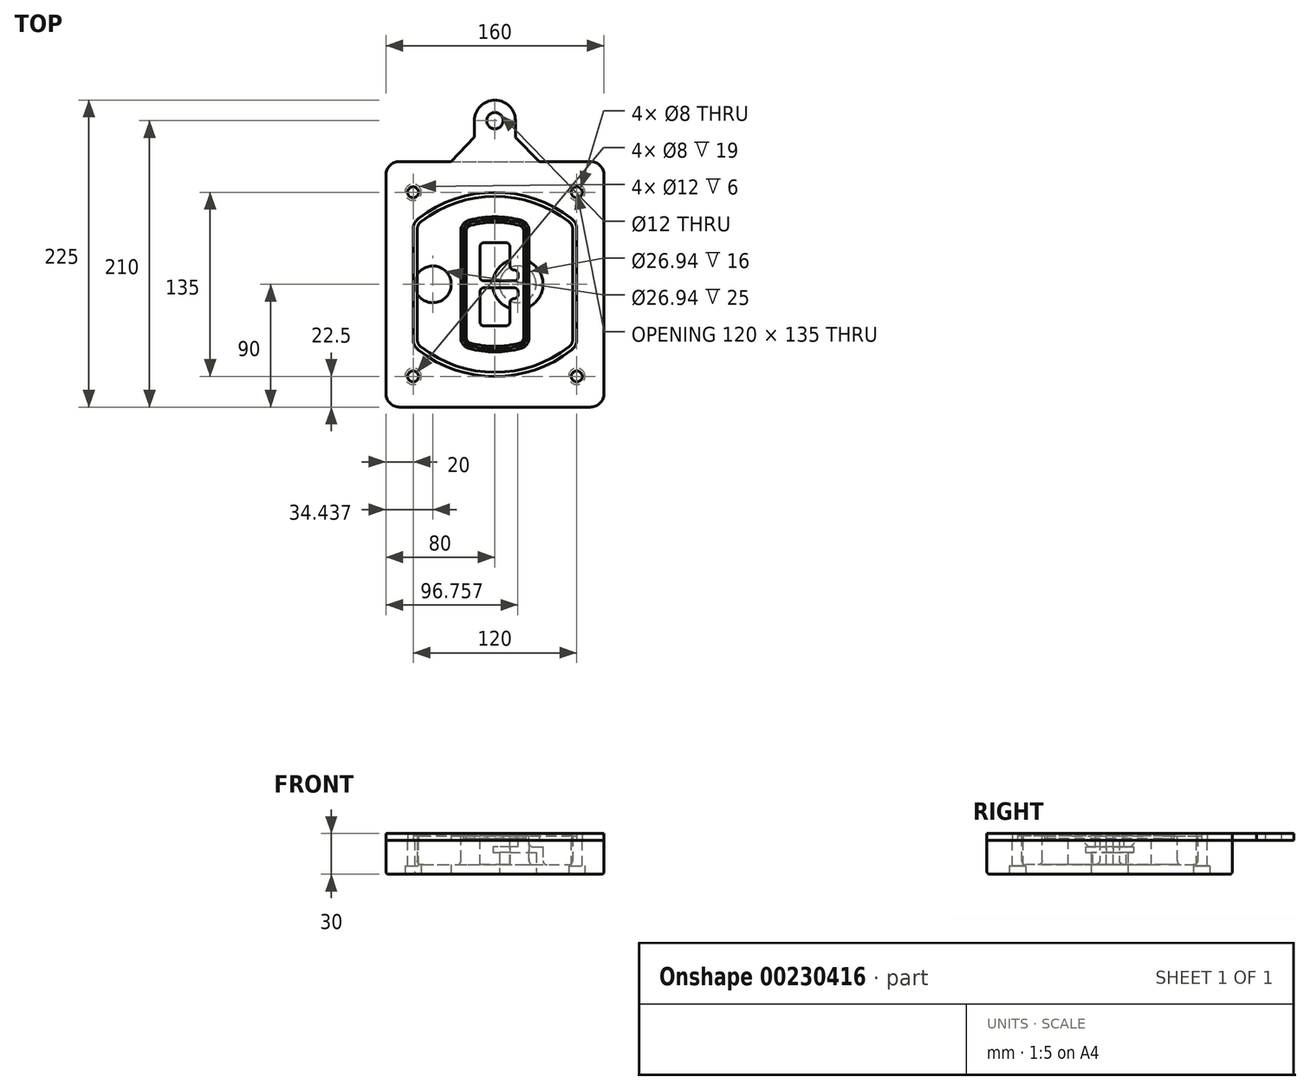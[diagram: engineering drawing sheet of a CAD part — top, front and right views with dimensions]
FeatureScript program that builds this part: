
annotation { "Feature Type Name" : "Feature", "Feature Type Description" : "" }
export const myFeature = defineFeature(function(context is Context, id is Id, definition is map)
    precondition{}
    {
        {
            var Q0;
            Q0=qCreatedBy(makeId("Top.planeOp"),FACE);
            var sketch = newSketch(context, id + "F0", { "sketchPlane" : qUnion([Q0])});
            skPoint(sketch, "E0.rect.middle", {"position": v(0, 0) * mm});
            skLineSegment(sketch, "E1.bottom", {"start": v(-70, -90) * mm, "end": v(70, -90) * mm});
            skLineSegment(sketch, "E1.top", {"start": v(-70, 90) * mm, "end": v(70, 90) * mm});
            skLineSegment(sketch, "E1.left", {"start": v(-80, -80) * mm, "end": v(-80, 80) * mm});
            skLineSegment(sketch, "E1.right", {"start": v(80, -80) * mm, "end": v(80, 80) * mm});
            skLineSegment(sketch, "E2", {"start": v(-80, 90) * mm, "end": v(80, -90) * mm, "construction": true});
            skLineSegment(sketch, "E3", {"start": v(80, 90) * mm, "end": v(-80, -90) * mm, "construction": true});
            skCircle(sketch, "E4", {"center": v(-60, 67.5) * mm, "radius": 4 * mm});
            skCircle(sketch, "E5", {"center": v(60, 67.5) * mm, "radius": 4 * mm});
            skCircle(sketch, "E6", {"center": v(60, -67.5) * mm, "radius": 4 * mm});
            skCircle(sketch, "E7", {"center": v(-60, -67.5) * mm, "radius": 4 * mm});
            skLineSegment(sketch, "E8", {"start": v(-60, 67.5) * mm, "end": v(60, 67.5) * mm, "construction": true});
            skLineSegment(sketch, "E9", {"start": v(60, 67.5) * mm, "end": v(60, -67.5) * mm, "construction": true});
            skLineSegment(sketch, "E10", {"start": v(60, -67.5) * mm, "end": v(-60, -67.5) * mm, "construction": true});
            skLineSegment(sketch, "E11", {"start": v(-60, -67.5) * mm, "end": v(-60, 67.5) * mm, "construction": true});
            skLineSegment(sketch, "E12", {"start": v(-60, 40.3) * mm, "end": v(-60, -40.3) * mm});
            skLineSegment(sketch, "E13", {"start": v(60, 40.3) * mm, "end": v(60, -40.3) * mm});
            skArc(sketch, "E14", {"start": v(56.15, 48.18) * mm, "mid": v(0, 67.5) * mm, "end": v(-56.15, 48.18) * mm});
            skArc(sketch, "E15", {"start": v(-56.15, -48.18) * mm, "mid": v(0, -67.5) * mm, "end": v(56.15, -48.18) * mm});
            skLineSegment(sketch, "E16", {"start": v(-60, 0) * mm, "end": v(60, 0) * mm, "construction": true});
            skPoint(sketch, "E17.visualSharp", {"position": v(-60, -45) * mm});
            skArc(sketch, "E17.filletArc", {"start": v(-60, -40.3) * mm, "mid": v(-58.99, -44.68) * mm, "end": v(-56.15, -48.18) * mm});
            skPoint(sketch, "E18.visualSharp", {"position": v(-60, 45) * mm});
            skArc(sketch, "E18.filletArc", {"start": v(-56.15, 48.18) * mm, "mid": v(-58.99, 44.68) * mm, "end": v(-60, 40.3) * mm});
            skPoint(sketch, "E19.visualSharp", {"position": v(60, 45) * mm});
            skArc(sketch, "E19.filletArc", {"start": v(60, 40.3) * mm, "mid": v(58.99, 44.68) * mm, "end": v(56.15, 48.18) * mm});
            skPoint(sketch, "E20.visualSharp", {"position": v(60, -45) * mm});
            skArc(sketch, "E20.filletArc", {"start": v(56.15, -48.18) * mm, "mid": v(58.99, -44.68) * mm, "end": v(60, -40.3) * mm});
            skPoint(sketch, "E21.visualSharp", {"position": v(-80, 90) * mm});
            skArc(sketch, "E21.filletArc", {"start": v(-70, 90) * mm, "mid": v(-77.07, 87.07) * mm, "end": v(-80, 80) * mm});
            skPoint(sketch, "E22.visualSharp", {"position": v(80, 90) * mm});
            skArc(sketch, "E22.filletArc", {"start": v(80, 80) * mm, "mid": v(77.07, 87.07) * mm, "end": v(70, 90) * mm});
            skPoint(sketch, "E23.visualSharp", {"position": v(80, -90) * mm});
            skArc(sketch, "E23.filletArc", {"start": v(70, -90) * mm, "mid": v(77.07, -87.07) * mm, "end": v(80, -80) * mm});
            skPoint(sketch, "E24.visualSharp", {"position": v(-80, -90) * mm});
            skArc(sketch, "E24.filletArc", {"start": v(-80, -80) * mm, "mid": v(-77.07, -87.07) * mm, "end": v(-70, -90) * mm});
            skArc(sketch, "E25.0", {"start": v(57, 40.3) * mm, "mid": v(56.3, 43.36) * mm, "end": v(54.3, 45.81) * mm});
            skLineSegment(sketch, "E25.1", {"start": v(57, 40.3) * mm, "end": v(57, -40.3) * mm});
            skArc(sketch, "E25.2", {"start": v(54.3, -45.81) * mm, "mid": v(56.3, -43.36) * mm, "end": v(57, -40.3) * mm});
            skArc(sketch, "E25.3", {"start": v(-54.3, -45.81) * mm, "mid": v(0, -64.5) * mm, "end": v(54.3, -45.81) * mm});
            skArc(sketch, "E25.4", {"start": v(-57, -40.3) * mm, "mid": v(-56.3, -43.36) * mm, "end": v(-54.3, -45.81) * mm});
            skArc(sketch, "E25.5", {"start": v(54.3, 45.81) * mm, "mid": v(0, 64.5) * mm, "end": v(-54.3, 45.81) * mm});
            skLineSegment(sketch, "E25.6", {"start": v(-57, 40.3) * mm, "end": v(-57, -40.3) * mm});
            skArc(sketch, "E25.7", {"start": v(-54.3, 45.81) * mm, "mid": v(-56.3, 43.36) * mm, "end": v(-57, 40.3) * mm});
            skArc(sketch, "E26.0", {"start": v(-58.62, 51.33) * mm, "mid": v(-62.58, 46.43) * mm, "end": v(-64, 40.3) * mm});
            skArc(sketch, "E26.1", {"start": v(58.62, 51.33) * mm, "mid": v(0, 71.5) * mm, "end": v(-58.62, 51.33) * mm});
            skArc(sketch, "E26.2", {"start": v(64, 40.3) * mm, "mid": v(62.58, 46.43) * mm, "end": v(58.62, 51.33) * mm});
            skLineSegment(sketch, "E26.3", {"start": v(64, 40.3) * mm, "end": v(64, -40.3) * mm});
            skArc(sketch, "E26.4", {"start": v(58.62, -51.33) * mm, "mid": v(62.58, -46.43) * mm, "end": v(64, -40.3) * mm});
            skLineSegment(sketch, "E26.5", {"start": v(-64, 40.3) * mm, "end": v(-64, -40.3) * mm});
            skArc(sketch, "E26.6", {"start": v(-58.62, -51.33) * mm, "mid": v(0, -71.5) * mm, "end": v(58.62, -51.33) * mm});
            skArc(sketch, "E26.7", {"start": v(-64, -40.3) * mm, "mid": v(-62.58, -46.43) * mm, "end": v(-58.62, -51.33) * mm});
            skSolve(sketch);
        }
        {
            var Q0;
            Q0=makeQuery(id+"F0.imprint","IMPRINT",FACE,{"disambiguationData":[TD([[makeQuery(id+"F0.imprint","IMPRINT",EDGE,{"derivedFrom":sQuery(id+"F0.wireOp",EDGE,"E1.bottom")}),1.0]])]});
            var Q1;
            Q1=makeQuery(id+"F0.imprint","IMPRINT",FACE,{"disambiguationData":[TD([[makeQuery(id+"F0.imprint","IMPRINT",EDGE,{"derivedFrom":sQuery(id+"F0.wireOp",EDGE,"E12")}),1.0]])]});
            var Q2;
            Q2=makeQuery(id+"F0.imprint","IMPRINT",FACE,{"disambiguationData":[TD([[makeQuery(id+"F0.imprint","IMPRINT",EDGE,{"derivedFrom":sQuery(id+"F0.wireOp",EDGE,"E25.0")}),1.0]])]});
            var Q3;
            Q3=makeQuery(id+"F0.imprint","IMPRINT",FACE,{"disambiguationData":[TD([[makeQuery(id+"F0.imprint","IMPRINT",EDGE,{"derivedFrom":sQuery(id+"F0.wireOp",EDGE,"E12")}),-1.0]])]});
            extrude(context, id + "F1", {"entities" : qUnion([Q0, Q1, Q2, Q3]), "oppositeDirection" : true, "depth" : 25 * mm});
        }
        {
            var Q0;
            Q0=makeQuery(id+"F0.imprint","IMPRINT",FACE,{"disambiguationData":[TD([[makeQuery(id+"F0.imprint","IMPRINT",EDGE,{"derivedFrom":sQuery(id+"F0.wireOp",EDGE,"E12")}),1.0]])]});
            extrude(context, id + "F2", {"entities" : qUnion([Q0]), "operationType" : NewBodyOperationType.ADD, "depth" : 3 * mm});
        }
        {
            var Q0;
            Q0=makeQuery(id+"F0.imprint","IMPRINT",FACE,{"disambiguationData":[TD([[makeQuery(id+"F0.imprint","IMPRINT",EDGE,{"derivedFrom":sQuery(id+"F0.wireOp",EDGE,"E25.0")}),1.0]])]});
            extrude(context, id + "F3", {"entities" : qUnion([Q0]), "operationType" : NewBodyOperationType.REMOVE, "oppositeDirection" : true, "depth" : 18 * mm});
        }
        {
            var Q0;
            Q0=makeQuery(id+"F2.opExtrude","CAP_FACE",FACE,{"disambiguationData":[OSD([sQuery(id+"F0.wireOp",EDGE,"E12"),sQuery(id+"F0.wireOp",EDGE,"E13"),sQuery(id+"F0.wireOp",EDGE,"E14"),sQuery(id+"F0.wireOp",EDGE,"E15"),sQuery(id+"F0.wireOp",EDGE,"E17.filletArc"),sQuery(id+"F0.wireOp",EDGE,"E18.filletArc"),sQuery(id+"F0.wireOp",EDGE,"E19.filletArc"),sQuery(id+"F0.wireOp",EDGE,"E20.filletArc"),sQuery(id+"F0.wireOp",EDGE,"E25.0"),sQuery(id+"F0.wireOp",EDGE,"E25.1"),sQuery(id+"F0.wireOp",EDGE,"E25.2"),sQuery(id+"F0.wireOp",EDGE,"E25.3"),sQuery(id+"F0.wireOp",EDGE,"E25.4"),sQuery(id+"F0.wireOp",EDGE,"E25.5"),sQuery(id+"F0.wireOp",EDGE,"E25.6"),sQuery(id+"F0.wireOp",EDGE,"E25.7")])],"isStart":false});
            var sketch = newSketch(context, id + "F4", { "sketchPlane" : qUnion([Q0])});
            skArc(sketch, "E27.0", {"start": v(-19.08, -46.97) * mm, "mid": v(0, -49.5) * mm, "end": v(19.08, -46.97) * mm});
            skArc(sketch, "E28.0", {"start": v(19.08, 46.97) * mm, "mid": v(0, 49.5) * mm, "end": v(-19.08, 46.97) * mm});
            skLineSegment(sketch, "E29", {"start": v(-25, 39.25) * mm, "end": v(-25, -39.25) * mm});
            skLineSegment(sketch, "E30", {"start": v(25, 39.25) * mm, "end": v(25, -39.25) * mm});
            skLineSegment(sketch, "E31", {"start": v(-25, 45.1) * mm, "end": v(25, 45.1) * mm, "construction": true});
            skLineSegment(sketch, "E32", {"start": v(-25, -45.1) * mm, "end": v(25, -45.1) * mm, "construction": true});
            skPoint(sketch, "E33.visualSharp", {"position": v(-25, 45.1) * mm});
            skArc(sketch, "E33.filletArc", {"start": v(-19.08, 46.97) * mm, "mid": v(-23.35, 44.11) * mm, "end": v(-25, 39.25) * mm});
            skPoint(sketch, "E34.visualSharp", {"position": v(25, 45.1) * mm});
            skArc(sketch, "E34.filletArc", {"start": v(25, 39.25) * mm, "mid": v(23.35, 44.11) * mm, "end": v(19.08, 46.97) * mm});
            skPoint(sketch, "E35.visualSharp", {"position": v(25, -45.1) * mm});
            skArc(sketch, "E35.filletArc", {"start": v(19.08, -46.97) * mm, "mid": v(23.35, -44.11) * mm, "end": v(25, -39.25) * mm});
            skPoint(sketch, "E36.visualSharp", {"position": v(-25, -45.1) * mm});
            skArc(sketch, "E36.filletArc", {"start": v(-25, -39.25) * mm, "mid": v(-23.35, -44.11) * mm, "end": v(-19.08, -46.97) * mm});
            skArc(sketch, "E37.0", {"start": v(54.3, 45.81) * mm, "mid": v(0, 64.5) * mm, "end": v(-54.3, 45.81) * mm});
            skArc(sketch, "E37.1", {"start": v(-54.3, 45.81) * mm, "mid": v(-56.3, 43.36) * mm, "end": v(-57, 40.3) * mm});
            skLineSegment(sketch, "E37.2", {"start": v(-57, 40.3) * mm, "end": v(-57, -40.3) * mm});
            skArc(sketch, "E37.3", {"start": v(-57, -40.3) * mm, "mid": v(-56.3, -43.36) * mm, "end": v(-54.3, -45.81) * mm});
            skArc(sketch, "E37.4", {"start": v(-54.3, -45.81) * mm, "mid": v(0, -64.5) * mm, "end": v(54.3, -45.81) * mm});
            skArc(sketch, "E37.5", {"start": v(54.3, -45.81) * mm, "mid": v(56.3, -43.36) * mm, "end": v(57, -40.3) * mm});
            skLineSegment(sketch, "E37.6", {"start": v(57, 40.3) * mm, "end": v(57, -40.3) * mm});
            skArc(sketch, "E37.7", {"start": v(57, 40.3) * mm, "mid": v(56.3, 43.36) * mm, "end": v(54.3, 45.81) * mm});
            skLineSegment(sketch, "E38.0", {"start": v(23, 39.25) * mm, "end": v(23, -39.25) * mm});
            skArc(sketch, "E38.1", {"start": v(18.56, -45.04) * mm, "mid": v(21.76, -42.9) * mm, "end": v(23, -39.25) * mm});
            skArc(sketch, "E38.2", {"start": v(-18.56, -45.04) * mm, "mid": v(0, -47.5) * mm, "end": v(18.56, -45.04) * mm});
            skArc(sketch, "E38.3", {"start": v(-23, -39.25) * mm, "mid": v(-21.76, -42.9) * mm, "end": v(-18.56, -45.04) * mm});
            skLineSegment(sketch, "E38.4", {"start": v(-23, 39.25) * mm, "end": v(-23, -39.25) * mm});
            skArc(sketch, "E38.5", {"start": v(23, 39.25) * mm, "mid": v(21.76, 42.9) * mm, "end": v(18.56, 45.04) * mm});
            skArc(sketch, "E38.6", {"start": v(-18.56, 45.04) * mm, "mid": v(-21.76, 42.9) * mm, "end": v(-23, 39.25) * mm});
            skArc(sketch, "E38.7", {"start": v(18.56, 45.04) * mm, "mid": v(0, 47.5) * mm, "end": v(-18.56, 45.04) * mm});
            skArc(sketch, "E39.0", {"start": v(21, 39.25) * mm, "mid": v(20.18, 41.68) * mm, "end": v(18.04, 43.1) * mm});
            skLineSegment(sketch, "E39.1", {"start": v(21, 39.25) * mm, "end": v(21, -39.25) * mm});
            skArc(sketch, "E39.2", {"start": v(18.04, -43.1) * mm, "mid": v(20.18, -41.68) * mm, "end": v(21, -39.25) * mm});
            skArc(sketch, "E39.3", {"start": v(-18.04, -43.1) * mm, "mid": v(0, -45.5) * mm, "end": v(18.04, -43.1) * mm});
            skArc(sketch, "E39.4", {"start": v(-21, -39.25) * mm, "mid": v(-20.18, -41.68) * mm, "end": v(-18.04, -43.1) * mm});
            skArc(sketch, "E39.5", {"start": v(18.04, 43.1) * mm, "mid": v(0, 45.5) * mm, "end": v(-18.04, 43.1) * mm});
            skLineSegment(sketch, "E39.6", {"start": v(-21, 39.25) * mm, "end": v(-21, -39.25) * mm});
            skArc(sketch, "E39.7", {"start": v(-18.04, 43.1) * mm, "mid": v(-20.18, 41.68) * mm, "end": v(-21, 39.25) * mm});
            skLineSegment(sketch, "E40", {"start": v(-25, 0) * mm, "end": v(25, 0) * mm, "construction": true});
            skLineSegment(sketch, "E41", {"start": v(-11, 5.5) * mm, "end": v(-11, 27.5) * mm});
            skLineSegment(sketch, "E42", {"start": v(-8, 30.5) * mm, "end": v(8, 30.5) * mm});
            skLineSegment(sketch, "E43", {"start": v(11, 27.5) * mm, "end": v(11, 13.5) * mm});
            skLineSegment(sketch, "E44", {"start": v(14, 10.5) * mm, "end": v(14, 10.5) * mm});
            skLineSegment(sketch, "E45", {"start": v(17, 7.5) * mm, "end": v(17, 5.5) * mm});
            skLineSegment(sketch, "E46", {"start": v(14, 2.5) * mm, "end": v(-8, 2.5) * mm});
            skPoint(sketch, "E47.visualSharp", {"position": v(-11, 30.5) * mm});
            skArc(sketch, "E47.filletArc", {"start": v(-8, 30.5) * mm, "mid": v(-10.12, 29.62) * mm, "end": v(-11, 27.5) * mm});
            skPoint(sketch, "E48.visualSharp", {"position": v(11, 30.5) * mm});
            skArc(sketch, "E48.filletArc", {"start": v(11, 27.5) * mm, "mid": v(10.12, 29.62) * mm, "end": v(8, 30.5) * mm});
            skPoint(sketch, "E49.visualSharp", {"position": v(11, 10.5) * mm});
            skArc(sketch, "E49.filletArc", {"start": v(11, 13.5) * mm, "mid": v(11.88, 11.38) * mm, "end": v(14, 10.5) * mm});
            skPoint(sketch, "E50.visualSharp", {"position": v(17, 10.5) * mm});
            skArc(sketch, "E50.filletArc", {"start": v(17, 7.5) * mm, "mid": v(16.12, 9.62) * mm, "end": v(14, 10.5) * mm});
            skPoint(sketch, "E51.visualSharp", {"position": v(17, 2.5) * mm});
            skArc(sketch, "E51.filletArc", {"start": v(14, 2.5) * mm, "mid": v(16.12, 3.38) * mm, "end": v(17, 5.5) * mm});
            skPoint(sketch, "E52.visualSharp", {"position": v(-11, 2.5) * mm});
            skArc(sketch, "E52.filletArc", {"start": v(-11, 5.5) * mm, "mid": v(-10.12, 3.38) * mm, "end": v(-8, 2.5) * mm});
            skLineSegment(sketch, "E53.0.MirrorCS", {"start": v(14, -2.5) * mm, "end": v(-8, -2.5) * mm});
            skArc(sketch, "E54.0.MirrorCS", {"start": v(-11, -5.5) * mm, "mid": v(-10.12, -3.38) * mm, "end": v(-8, -2.5) * mm});
            skLineSegment(sketch, "E55.0.MirrorCS", {"start": v(-11, -5.5) * mm, "end": v(-11, -27.5) * mm});
            skArc(sketch, "E56.0.MirrorCS", {"start": v(-8, -30.5) * mm, "mid": v(-10.12, -29.62) * mm, "end": v(-11, -27.5) * mm});
            skLineSegment(sketch, "E57.0.MirrorCS", {"start": v(-8, -30.5) * mm, "end": v(8, -30.5) * mm});
            skArc(sketch, "E58.0.MirrorCS", {"start": v(11, -27.5) * mm, "mid": v(10.12, -29.62) * mm, "end": v(8, -30.5) * mm});
            skLineSegment(sketch, "E59.0.MirrorCS", {"start": v(11, -27.5) * mm, "end": v(11, -13.5) * mm});
            skArc(sketch, "E60.0.MirrorCS", {"start": v(11, -13.5) * mm, "mid": v(11.88, -11.38) * mm, "end": v(14, -10.5) * mm});
            skArc(sketch, "E61.0.MirrorCS", {"start": v(17, -7.5) * mm, "mid": v(16.12, -9.62) * mm, "end": v(14, -10.5) * mm});
            skLineSegment(sketch, "E62.0.MirrorCS", {"start": v(17, -7.5) * mm, "end": v(17, -5.5) * mm});
            skArc(sketch, "E63.0.MirrorCS", {"start": v(14, -2.5) * mm, "mid": v(16.12, -3.38) * mm, "end": v(17, -5.5) * mm});
            skSolve(sketch);
        }
        {
            var Q0;
            Q0=makeQuery(id+"F4.imprint","IMPRINT",FACE,{"disambiguationData":[TD([[makeQuery(id+"F4.imprint","IMPRINT",EDGE,{"derivedFrom":sQuery(id+"F4.wireOp",EDGE,"E27.0")}),1.0]])]});
            var Q1;
            Q1=makeQuery(id+"F4.imprint","IMPRINT",FACE,{"disambiguationData":[TD([[makeQuery(id+"F4.imprint","IMPRINT",EDGE,{"derivedFrom":sQuery(id+"F4.wireOp",EDGE,"E38.0")}),-1.0]])]});
            var Q2;
            Q2=makeQuery(id+"F4.imprint","IMPRINT",FACE,{"disambiguationData":[TD([[makeQuery(id+"F4.imprint","IMPRINT",EDGE,{"derivedFrom":sQuery(id+"F4.wireOp",EDGE,"E39.0")}),1.0]])]});
            extrude(context, id + "F5", {"entities" : qUnion([Q0, Q1, Q2]), "operationType" : NewBodyOperationType.ADD, "endBound" : BoundingType.UP_TO_NEXT, "oppositeDirection" : true, "depth" : 25 * mm});
        }
        {
            var Q0;
            Q0=makeQuery(id+"F4.imprint","IMPRINT",FACE,{"disambiguationData":[TD([[makeQuery(id+"F4.imprint","IMPRINT",EDGE,{"derivedFrom":sQuery(id+"F4.wireOp",EDGE,"E38.0")}),-1.0]])]});
            extrude(context, id + "F6", {"entities" : qUnion([Q0]), "operationType" : NewBodyOperationType.REMOVE, "oppositeDirection" : true, "depth" : 2 * mm});
        }
        {
            var Q0;
            Q0=makeQuery(id+"F1.opExtrude","CAP_FACE",FACE,{"disambiguationData":[OSD([sQuery(id+"F0.wireOp",EDGE,"E1.bottom"),sQuery(id+"F0.wireOp",EDGE,"E1.top"),sQuery(id+"F0.wireOp",EDGE,"E1.left"),sQuery(id+"F0.wireOp",EDGE,"E1.right"),sQuery(id+"F0.wireOp",EDGE,"E4"),sQuery(id+"F0.wireOp",EDGE,"E5"),sQuery(id+"F0.wireOp",EDGE,"E6"),sQuery(id+"F0.wireOp",EDGE,"E7"),sQuery(id+"F0.wireOp",EDGE,"E21.filletArc"),sQuery(id+"F0.wireOp",EDGE,"E22.filletArc"),sQuery(id+"F0.wireOp",EDGE,"E23.filletArc"),sQuery(id+"F0.wireOp",EDGE,"E24.filletArc")])],"isStart":false});
            var sketch = newSketch(context, id + "F7", { "sketchPlane" : qUnion([Q0])});
            skCircle(sketch, "E64", {"center": v(16.76, 0) * mm, "radius": 13.47 * mm});
            skCircle(sketch, "E65", {"center": v(-45.56, 0) * mm, "radius": 13.47 * mm});
            skLineSegment(sketch, "E66", {"start": v(80, 0) * mm, "end": v(-80, 0) * mm});
            skCircle(sketch, "E67", {"center": v(16.76, 0) * mm, "radius": 18.47 * mm});
            skCircle(sketch, "E68", {"center": v(60, -67.5) * mm, "radius": 6 * mm});
            skCircle(sketch, "E69", {"center": v(-60, -67.5) * mm, "radius": 6 * mm});
            skCircle(sketch, "E70", {"center": v(-60, 67.5) * mm, "radius": 6 * mm});
            skCircle(sketch, "E71", {"center": v(60, 67.5) * mm, "radius": 6 * mm});
            skSolve(sketch);
        }
        {
            var Q0;
            {var subQ1=sQuery(id+"F7.wireOp",EDGE,"E66");var subQ4=sQuery(id+"F7.wireOp",EDGE,"E64");var subQ6=makeQuery(id+"F7.imprint","INTERSECT",VERTEX,{"disambiguationData":[OD(0.0)],"derivedFrom":[subQ4,subQ1]});Q0=makeQuery(id+"F7.imprint","IMPRINT",FACE,{"disambiguationData":[TD([[makeQuery(id+"F7.imprint","IMPRINT",EDGE,{"disambiguationData":[TD([[subQ6,-1.0]])],"derivedFrom":subQ4}),-1.0]])]});}
            var Q1;
            {var subQ0=sQuery(id+"F7.wireOp",EDGE,"E66");var subQ1=sQuery(id+"F7.wireOp",EDGE,"E64");var subQ3=makeQuery(id+"F7.imprint","INTERSECT",VERTEX,{"disambiguationData":[OD(0.0)],"derivedFrom":[subQ1,subQ0]});Q1=makeQuery(id+"F7.imprint","IMPRINT",FACE,{"disambiguationData":[TD([[makeQuery(id+"F7.imprint","IMPRINT",EDGE,{"disambiguationData":[TD([[subQ3,-1.0]])],"derivedFrom":subQ1}),1.0]])]});}
            var Q2;
            {var subQ0=sQuery(id+"F7.wireOp",EDGE,"E66");var subQ1=sQuery(id+"F7.wireOp",EDGE,"E64");var subQ3=makeQuery(id+"F7.imprint","INTERSECT",VERTEX,{"disambiguationData":[OD(0.0)],"derivedFrom":[subQ1,subQ0]});Q2=makeQuery(id+"F7.imprint","IMPRINT",FACE,{"disambiguationData":[TD([[makeQuery(id+"F7.imprint","IMPRINT",EDGE,{"disambiguationData":[TD([[subQ3,1.0]])],"derivedFrom":subQ1}),1.0]])]});}
            var Q3;
            {var subQ1=sQuery(id+"F7.wireOp",EDGE,"E66");var subQ4=sQuery(id+"F7.wireOp",EDGE,"E64");var subQ6=makeQuery(id+"F7.imprint","INTERSECT",VERTEX,{"disambiguationData":[OD(0.0)],"derivedFrom":[subQ4,subQ1]});Q3=makeQuery(id+"F7.imprint","IMPRINT",FACE,{"disambiguationData":[TD([[makeQuery(id+"F7.imprint","IMPRINT",EDGE,{"disambiguationData":[TD([[subQ6,1.0]])],"derivedFrom":subQ4}),-1.0]])]});}
            extrude(context, id + "F8", {"entities" : qUnion([Q0, Q1, Q2, Q3]), "operationType" : NewBodyOperationType.ADD, "oppositeDirection" : true, "depth" : 20 * mm});
        }
        {
            var Q0;
            {var subQ0=sQuery(id+"F7.wireOp",EDGE,"E66");var subQ1=sQuery(id+"F7.wireOp",EDGE,"E64");var subQ3=makeQuery(id+"F7.imprint","INTERSECT",VERTEX,{"disambiguationData":[OD(0.0)],"derivedFrom":[subQ1,subQ0]});Q0=makeQuery(id+"F7.imprint","IMPRINT",FACE,{"disambiguationData":[TD([[makeQuery(id+"F7.imprint","IMPRINT",EDGE,{"disambiguationData":[TD([[subQ3,-1.0]])],"derivedFrom":subQ1}),1.0]])]});}
            var Q1;
            {var subQ0=sQuery(id+"F7.wireOp",EDGE,"E66");var subQ1=sQuery(id+"F7.wireOp",EDGE,"E64");var subQ3=makeQuery(id+"F7.imprint","INTERSECT",VERTEX,{"disambiguationData":[OD(0.0)],"derivedFrom":[subQ1,subQ0]});Q1=makeQuery(id+"F7.imprint","IMPRINT",FACE,{"disambiguationData":[TD([[makeQuery(id+"F7.imprint","IMPRINT",EDGE,{"disambiguationData":[TD([[subQ3,1.0]])],"derivedFrom":subQ1}),1.0]])]});}
            extrude(context, id + "F9", {"entities" : qUnion([Q0, Q1]), "operationType" : NewBodyOperationType.REMOVE, "oppositeDirection" : true, "depth" : 16 * mm});
        }
        {
            var Q0;
            {var subQ0=sQuery(id+"F7.wireOp",EDGE,"E66");var subQ1=sQuery(id+"F7.wireOp",EDGE,"E65");var subQ3=makeQuery(id+"F7.imprint","INTERSECT",VERTEX,{"disambiguationData":[OD(0.0)],"derivedFrom":[subQ1,subQ0]});Q0=makeQuery(id+"F7.imprint","IMPRINT",FACE,{"disambiguationData":[TD([[makeQuery(id+"F7.imprint","IMPRINT",EDGE,{"disambiguationData":[TD([[subQ3,-1.0]])],"derivedFrom":subQ1}),1.0]])]});}
            var Q1;
            {var subQ0=sQuery(id+"F7.wireOp",EDGE,"E66");var subQ1=sQuery(id+"F7.wireOp",EDGE,"E65");var subQ3=makeQuery(id+"F7.imprint","INTERSECT",VERTEX,{"disambiguationData":[OD(0.0)],"derivedFrom":[subQ1,subQ0]});Q1=makeQuery(id+"F7.imprint","IMPRINT",FACE,{"disambiguationData":[TD([[makeQuery(id+"F7.imprint","IMPRINT",EDGE,{"disambiguationData":[TD([[subQ3,1.0]])],"derivedFrom":subQ1}),1.0]])]});}
            extrude(context, id + "F10", {"entities" : qUnion([Q0, Q1]), "operationType" : NewBodyOperationType.REMOVE, "oppositeDirection" : true, "depth" : 25 * mm});
        }
        {
            var Q0;
            Q0=makeQuery(id+"F7.imprint","IMPRINT",FACE,{"disambiguationData":[TD([[makeQuery(id+"F7.imprint","IMPRINT",EDGE,{"derivedFrom":sQuery(id+"F7.wireOp",EDGE,"E68")}),1.0]])]});
            var Q1;
            Q1=makeQuery(id+"F7.imprint","IMPRINT",FACE,{"disambiguationData":[TD([[makeQuery(id+"F7.imprint","IMPRINT",EDGE,{"derivedFrom":makeQuery(id+"F1.opExtrude","CAP_EDGE",EDGE,{"disambiguationData":[OSD([sQuery(id+"F0.wireOp",EDGE,"E5")])],"isStart":false})}),-1.0]])]});
            var Q2;
            Q2=makeQuery(id+"F7.imprint","IMPRINT",FACE,{"disambiguationData":[TD([[makeQuery(id+"F7.imprint","IMPRINT",EDGE,{"derivedFrom":sQuery(id+"F7.wireOp",EDGE,"E69")}),1.0]])]});
            var Q3;
            Q3=makeQuery(id+"F7.imprint","IMPRINT",FACE,{"disambiguationData":[TD([[makeQuery(id+"F7.imprint","IMPRINT",EDGE,{"derivedFrom":makeQuery(id+"F1.opExtrude","CAP_EDGE",EDGE,{"disambiguationData":[OSD([sQuery(id+"F0.wireOp",EDGE,"E4")])],"isStart":false})}),-1.0]])]});
            var Q4;
            Q4=makeQuery(id+"F7.imprint","IMPRINT",FACE,{"disambiguationData":[TD([[makeQuery(id+"F7.imprint","IMPRINT",EDGE,{"derivedFrom":sQuery(id+"F7.wireOp",EDGE,"E70")}),1.0]])]});
            var Q5;
            Q5=makeQuery(id+"F7.imprint","IMPRINT",FACE,{"disambiguationData":[TD([[makeQuery(id+"F7.imprint","IMPRINT",EDGE,{"derivedFrom":makeQuery(id+"F1.opExtrude","CAP_EDGE",EDGE,{"disambiguationData":[OSD([sQuery(id+"F0.wireOp",EDGE,"E7")])],"isStart":false})}),-1.0]])]});
            var Q6;
            Q6=makeQuery(id+"F7.imprint","IMPRINT",FACE,{"disambiguationData":[TD([[makeQuery(id+"F7.imprint","IMPRINT",EDGE,{"derivedFrom":sQuery(id+"F7.wireOp",EDGE,"E71")}),1.0]])]});
            var Q7;
            Q7=makeQuery(id+"F7.imprint","IMPRINT",FACE,{"disambiguationData":[TD([[makeQuery(id+"F7.imprint","IMPRINT",EDGE,{"derivedFrom":makeQuery(id+"F1.opExtrude","CAP_EDGE",EDGE,{"disambiguationData":[OSD([sQuery(id+"F0.wireOp",EDGE,"E6")])],"isStart":false})}),-1.0]])]});
            extrude(context, id + "F11", {"entities" : qUnion([Q0, Q1, Q2, Q3, Q4, Q5, Q6, Q7]), "operationType" : NewBodyOperationType.REMOVE, "oppositeDirection" : true, "depth" : 6 * mm});
        }
        {
            var Q0;
            Q0=makeQuery(id+"F9.boolean.opBoolean","COPY",FACE,{"derivedFrom":makeQuery(id+"F9.opExtrude","CAP_FACE",FACE,{"disambiguationData":[OSD([sQuery(id+"F7.wireOp",EDGE,"E64")])],"isStart":false})});
            var sketch = newSketch(context, id + "F12", { "sketchPlane" : qUnion([Q0])});
            skArc(sketch, "E72.0", {"start": v(11, 17.55) * mm, "mid": v(2.57, 11.82) * mm, "end": v(-1.54, 2.5) * mm});
            skArc(sketch, "E72.1", {"start": v(-1.54, -2.5) * mm, "mid": v(2.57, -11.82) * mm, "end": v(11, -17.55) * mm});
            skLineSegment(sketch, "E73", {"start": v(-1.54, -2.5) * mm, "end": v(14, -2.5) * mm});
            skLineSegment(sketch, "E74.0", {"start": v(14, 2.5) * mm, "end": v(-1.54, 2.5) * mm});
            skArc(sketch, "E74.1", {"start": v(14, 2.5) * mm, "mid": v(16.12, 3.38) * mm, "end": v(17, 5.5) * mm});
            skLineSegment(sketch, "E74.2", {"start": v(17, 7.5) * mm, "end": v(17, 5.5) * mm});
            skArc(sketch, "E74.3", {"start": v(17, 7.5) * mm, "mid": v(16.12, 9.62) * mm, "end": v(14, 10.5) * mm});
            skArc(sketch, "E74.4", {"start": v(11, 13.5) * mm, "mid": v(11.88, 11.38) * mm, "end": v(14, 10.5) * mm});
            skLineSegment(sketch, "E74.5", {"start": v(11, 17.55) * mm, "end": v(11, 13.5) * mm});
            skLineSegment(sketch, "E74.7", {"start": v(14, -2.5) * mm, "end": v(-1.54, -2.5) * mm});
            skArc(sketch, "E74.8", {"start": v(14, -2.5) * mm, "mid": v(16.12, -3.38) * mm, "end": v(17, -5.5) * mm});
            skLineSegment(sketch, "E74.9", {"start": v(17, -7.5) * mm, "end": v(17, -5.5) * mm});
            skArc(sketch, "E74.10", {"start": v(17, -7.5) * mm, "mid": v(16.12, -9.62) * mm, "end": v(14, -10.5) * mm});
            skArc(sketch, "E74.11", {"start": v(11, -13.5) * mm, "mid": v(11.88, -11.38) * mm, "end": v(14, -10.5) * mm});
            skLineSegment(sketch, "E74.12", {"start": v(11, -17.55) * mm, "end": v(11, -13.5) * mm});
            skPoint(sketch, "E75.orphan", {"position": v(11, -27.5) * mm});
            skPoint(sketch, "E76.orphan", {"position": v(-8, -2.5) * mm});
            skPoint(sketch, "E77.orphan", {"position": v(-8, 2.5) * mm});
            skPoint(sketch, "E78.orphan", {"position": v(11, 27.5) * mm});
            skSolve(sketch);
        }
        {
            var Q0;
            {var subQ7=sQuery(id+"F12.wireOp",EDGE,"E72.0");var subQ14=sQuery(id+"F12.wireOp",EDGE,"E72.1");var subQ16=sQuery(id+"F12.wireOp",EDGE,"E74.1");var subQ18=sQuery(id+"F12.wireOp",EDGE,"E74.8");Q0=qUnion([makeQuery(id+"F12.imprint","IMPRINT",FACE,{"disambiguationData":[TD([[makeQuery(id+"F12.imprint","IMPRINT",EDGE,{"derivedFrom":subQ7}),1.0]])]}),makeQuery(id+"F12.imprint","IMPRINT",FACE,{"disambiguationData":[TD([[makeQuery(id+"F12.imprint","IMPRINT",EDGE,{"derivedFrom":subQ14}),1.0]])]}),makeQuery(id+"F12.imprint","IMPRINT",FACE,{"disambiguationData":[TD([[makeQuery(id+"F12.imprint","IMPRINT",EDGE,{"derivedFrom":subQ16}),1.0]])]}),makeQuery(id+"F12.imprint","IMPRINT",FACE,{"disambiguationData":[TD([[makeQuery(id+"F12.imprint","IMPRINT",EDGE,{"derivedFrom":subQ18}),-1.0]])]})]);}
            var Q1;
            Q1=makeQuery(id+"F5.boolean.opBoolean","SPLIT",FACE,{"disambiguationData":[TD([makeQuery(id+"F5.opExtrude","SWEPT_FACE",FACE,{"disambiguationData":[OSD([sQuery(id+"F4.wireOp",EDGE,"E41")])]})])],"derivedFrom":makeQuery(id+"F3.boolean.opBoolean","COPY",FACE,{"derivedFrom":makeQuery(id+"F3.opExtrude","CAP_FACE",FACE,{"disambiguationData":[OSD([sQuery(id+"F0.wireOp",EDGE,"E25.0"),sQuery(id+"F0.wireOp",EDGE,"E25.1"),sQuery(id+"F0.wireOp",EDGE,"E25.2"),sQuery(id+"F0.wireOp",EDGE,"E25.3"),sQuery(id+"F0.wireOp",EDGE,"E25.4"),sQuery(id+"F0.wireOp",EDGE,"E25.5"),sQuery(id+"F0.wireOp",EDGE,"E25.6"),sQuery(id+"F0.wireOp",EDGE,"E25.7")])],"isStart":false})})});
            extrude(context, id + "F13", {"entities" : qUnion([Q0]), "operationType" : NewBodyOperationType.REMOVE, "endBound" : BoundingType.UP_TO_SURFACE, "endBoundEntityFace" : qUnion([Q1]), "depth" : 25 * mm});
        }
        {
            var Q0;
            Q0=makeQuery(id+"F3.boolean.opBoolean","COPY",EDGE,{"derivedFrom":makeQuery(id+"F3.opExtrude","CAP_EDGE",EDGE,{"disambiguationData":[OSD([sQuery(id+"F0.wireOp",EDGE,"E25.6")])],"isStart":false})});
            var Q1;
            Q1=makeQuery(id+"F8.boolean.opBoolean","INTERSECT",EDGE,{"derivedFrom":[makeQuery(id+"F5.opExtrude","SWEPT_FACE",FACE,{"disambiguationData":[OSD([sQuery(id+"F4.wireOp",EDGE,"E30")])]}),makeQuery(id+"F8.opExtrude","CAP_FACE",FACE,{"disambiguationData":[OSD([sQuery(id+"F7.wireOp",EDGE,"E67")])],"isStart":false})]});
            var Q2;
            Q2=makeQuery(id+"F8.boolean.opBoolean","INTERSECT",EDGE,{"disambiguationData":[OD(1.0)],"derivedFrom":[makeQuery(id+"F5.opExtrude","SWEPT_FACE",FACE,{"disambiguationData":[OSD([sQuery(id+"F4.wireOp",EDGE,"E30")])]}),makeQuery(id+"F8.opExtrude","SWEPT_FACE",FACE,{"disambiguationData":[OSD([sQuery(id+"F7.wireOp",EDGE,"E67")])]})]});
            var Q3;
            {var subQ0=sQuery(id+"F4.wireOp",EDGE,"E30");Q3=makeQuery(id+"F8.boolean.opBoolean","SPLIT",EDGE,{"disambiguationData":[TD([makeQuery(id+"F5.opExtrude","SWEPT_FACE",FACE,{"disambiguationData":[OSD([sQuery(id+"F4.wireOp",EDGE,"E35.filletArc")])]})])],"derivedFrom":makeQuery(id+"F5.opExtrude","CAP_EDGE",EDGE,{"disambiguationData":[OSD([subQ0])],"isStart":false})});}
            var Q4;
            {var subQ0=sQuery(id+"F0.wireOp",EDGE,"E25.7");var subQ1=sQuery(id+"F0.wireOp",EDGE,"E25.1");var subQ2=sQuery(id+"F0.wireOp",EDGE,"E25.6");var subQ3=sQuery(id+"F0.wireOp",EDGE,"E25.5");var subQ4=sQuery(id+"F0.wireOp",EDGE,"E25.4");var subQ5=sQuery(id+"F0.wireOp",EDGE,"E25.0");var subQ6=sQuery(id+"F0.wireOp",EDGE,"E25.2");var subQ7=sQuery(id+"F0.wireOp",EDGE,"E25.3");Q4=makeQuery(id+"F8.boolean.opBoolean","INTERSECT",EDGE,{"derivedFrom":[makeQuery(id+"F5.boolean.opBoolean","SPLIT",FACE,{"disambiguationData":[TD([makeQuery(id+"F2.opExtrude","SWEPT_FACE",FACE,{"disambiguationData":[OSD([subQ5])]})])],"derivedFrom":makeQuery(id+"F3.boolean.opBoolean","COPY",FACE,{"derivedFrom":makeQuery(id+"F3.opExtrude","CAP_FACE",FACE,{"disambiguationData":[OSD([subQ5,subQ1,subQ6,subQ7,subQ4,subQ3,subQ2,subQ0])],"isStart":false})})}),makeQuery(id+"F8.opExtrude","SWEPT_FACE",FACE,{"disambiguationData":[OSD([sQuery(id+"F7.wireOp",EDGE,"E67")])]})]});}
            var Q5;
            Q5=makeQuery(id+"F8.boolean.opBoolean","INTERSECT",EDGE,{"disambiguationData":[OD(0.0)],"derivedFrom":[makeQuery(id+"F5.opExtrude","SWEPT_FACE",FACE,{"disambiguationData":[OSD([sQuery(id+"F4.wireOp",EDGE,"E30")])]}),makeQuery(id+"F8.opExtrude","SWEPT_FACE",FACE,{"disambiguationData":[OSD([sQuery(id+"F7.wireOp",EDGE,"E67")])]})]});
            fillet(context, id + "F14", {"entities" : qUnion([Q0, Q1, Q2, Q3, Q4, Q5]), "radius" : 3 * mm, "tangentPropagation" : true, "allowEdgeOverflow" : false});
        }
        {
            var Q0;
            Q0=makeQuery(id+"F1.opExtrude","CAP_EDGE",EDGE,{"disambiguationData":[OSD([sQuery(id+"F0.wireOp",EDGE,"E1.bottom")])],"isStart":false});
            fillet(context, id + "F15", {"entities" : qUnion([Q0]), "radius" : 2 * mm, "tangentPropagation" : true, "allowEdgeOverflow" : false});
        }
        {
            var Q0;
            {var subQ0=sQuery(id+"F0.wireOp",EDGE,"E22.filletArc");var subQ1=sQuery(id+"F0.wireOp",EDGE,"E7");var subQ2=sQuery(id+"F0.wireOp",EDGE,"E6");var subQ3=sQuery(id+"F0.wireOp",EDGE,"E5");var subQ4=sQuery(id+"F0.wireOp",EDGE,"E4");var subQ5=sQuery(id+"F0.wireOp",EDGE,"E1.bottom");var subQ6=sQuery(id+"F0.wireOp",EDGE,"E21.filletArc");var subQ7=sQuery(id+"F0.wireOp",EDGE,"E1.top");var subQ8=sQuery(id+"F0.wireOp",EDGE,"E1.left");var subQ9=sQuery(id+"F0.wireOp",EDGE,"E1.right");var subQ10=sQuery(id+"F0.wireOp",EDGE,"E23.filletArc");var subQ11=sQuery(id+"F0.wireOp",EDGE,"E24.filletArc");Q0=makeQuery(id+"F2.boolean.opBoolean","SPLIT",FACE,{"disambiguationData":[TD([makeQuery(id+"F1.opExtrude","SWEPT_FACE",FACE,{"disambiguationData":[OSD([subQ5])]})])],"derivedFrom":makeQuery(id+"F1.opExtrude","CAP_FACE",FACE,{"disambiguationData":[OSD([subQ5,subQ7,subQ8,subQ9,subQ4,subQ3,subQ2,subQ1,subQ6,subQ0,subQ10,subQ11])],"isStart":true})});}
            var sketch = newSketch(context, id + "F16", { "sketchPlane" : qUnion([Q0])});
            skLineSegment(sketch, "E79", {"start": v(-80, 0) * mm, "end": v(80, 0) * mm, "construction": true});
            skLineSegment(sketch, "E80", {"start": v(0, 90) * mm, "end": v(0, 120) * mm, "construction": true});
            skCircle(sketch, "E81", {"center": v(0, 120) * mm, "radius": 6 * mm});
            skArc(sketch, "E82", {"start": v(15, 120) * mm, "mid": v(0, 135) * mm, "end": v(-15, 120) * mm});
            skLineSegment(sketch, "E83", {"start": v(-15, 120) * mm, "end": v(-15, 108) * mm});
            skLineSegment(sketch, "E84", {"start": v(-15, 108) * mm, "end": v(-32.35, 90) * mm});
            skLineSegment(sketch, "E85", {"start": v(15, 120) * mm, "end": v(15, 107.68) * mm});
            skLineSegment(sketch, "E86", {"start": v(15, 107.68) * mm, "end": v(32.68, 90) * mm});
            skArc(sketch, "E87.MirrorCS", {"start": v(15, -120) * mm, "mid": v(0, -135) * mm, "end": v(-15, -120) * mm});
            skLineSegment(sketch, "E88.MirrorCS", {"start": v(15, -120) * mm, "end": v(15, -107.68) * mm});
            skLineSegment(sketch, "E89.MirrorCS", {"start": v(15, -107.68) * mm, "end": v(32.68, -90) * mm});
            skLineSegment(sketch, "E90.MirrorCS", {"start": v(-15, -108) * mm, "end": v(-32.35, -90) * mm});
            skLineSegment(sketch, "E91.MirrorCS", {"start": v(-15, -120) * mm, "end": v(-15, -108) * mm});
            skCircle(sketch, "E92.MirrorC", {"center": v(0, -120) * mm, "radius": 6 * mm});
            skLineSegment(sketch, "E93.MirrorCS", {"start": v(0, -90) * mm, "end": v(0, -120) * mm, "construction": true});
            skLineSegment(sketch, "E94", {"start": v(-32.35, 90) * mm, "end": v(32.68, 90) * mm});
            skLineSegment(sketch, "E95", {"start": v(-32.35, -90) * mm, "end": v(32.68, -90) * mm});
            skSolve(sketch);
        }
        {
            var Q0;
            Q0=makeQuery(id+"F16.imprint","IMPRINT",FACE,{"disambiguationData":[TD([[makeQuery(id+"F16.imprint","IMPRINT",EDGE,{"derivedFrom":sQuery(id+"F16.wireOp",EDGE,"E81")}),-1.0]])]});
            var Q1;
            {var subQ4=sQuery(id+"F16.wireOp",EDGE,"E94");Q1=makeQuery(id+"F16.imprint","IMPRINT",FACE,{"disambiguationData":[TD([[makeQuery(id+"F16.imprint","IMPRINT",EDGE,{"derivedFrom":subQ4}),-1.0]])]});}
            var Q2;
            Q2=makeQuery(id+"F16.imprint","IMPRINT",FACE,{"disambiguationData":[TD([[makeQuery(id+"F16.imprint","IMPRINT",EDGE,{"derivedFrom":sQuery(id+"F16.wireOp",EDGE,"E87.MirrorCS")}),-1.0]])]});
            extrude(context, id + "F17", {"entities" : qUnion([Q0, Q1, Q2]), "depth" : 5 * mm});
        }
    });
